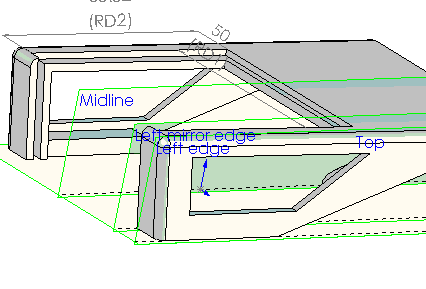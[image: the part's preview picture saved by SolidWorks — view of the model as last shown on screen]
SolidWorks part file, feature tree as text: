
SOLIDWORKS PART (.sldprt)
format: sldprt  version: not decoded by parser v0  size: 412,160 bytes
history: native  units: mm
features: sketch x11, extrude x6, cut_extrude x5, plane x3, fillet x2, mirror x1 + 1 further entry (+9 scaffold rows collapsed)
feature tree (38):
  "Annotations"  RD1=50mm RD2=55.020735mm
  scaffold x9  (default folders/planes/origin — collapsed)
  plane  "Midline"
  plane  "Left edge"  Offset=30.4mm
  plane  "Left mirror edge"  Offset=22mm
  sketch  "Sketch1"  dims[c1.D1=67.88mm c1.D2=33.429mm c1.D3=67.88mm c2.D3=160.0deg c2.D4=25.0mm c2.D5=25.0mm c3.D5=100.0deg c3.D6=25.0mm]
  extrude  "Extrude2"  Depth=2mm
  sketch  "Sketch3"  dims[D1=1.5mm]
  extrude  "Extrude3"  [1 undecoded]
  sketch  "Sketch5"  dims[c1.D1=~23.472852mm c2.D1=~1.335299deg c3.D1=2.0mm c3.D2=~2.004887mm c3.D3=~23.44485mm c4.D1=2.0mm c4.D3=~23.44485mm c5.D3=100.0deg c6.D3=~23.44485mm c7.D3=~0.228426deg c8.D3=~23.44485mm c9.D3=~0.228426deg c10.D3=~23.406929mm c11.D3=~0.03502deg c12.D3=~23.406929mm c13.D3=~0.03502deg c14.D3=2.0mm c14.D4=2.0mm c14.D5=~23.46153mm]
  extrude  "Extrude5"  [1 undecoded]
  sketch  "Sketch11"  dims[D1=4.0mm]
  extrude  "Extrude8"  Depth=5mm
  sketch  "Sketch12"  dims[c1.D1=2.5mm c1.D2=25.0mm c1.D3=30.0mm c2.D2=3.0mm c2.D4=2.0mm c2.D5=50.0mm]
  cut_extrude  "Sideport cut"  Depth=4mm
  mirror  "Mirror1"
  sketch  "Sketch9"  dims[c1.D1=25.0mm c1.D2=40.0mm c1.D3=50.0mm c1.D4=7.0mm c2.D2=25.0mm c2.D4=~4.389902mm c3.D4=90.0deg c4.D4=5.0mm]
  cut_extrude  "Viewport cutout"  Depth=5mm
  sketch  "Sketch10"  dims[c1.D1=4.0mm c1.D2=2.0mm c1.D3=40.0mm c2.D3=~0.615732deg c3.D3=4.0mm c3.D4=4.0mm c3.D5=2.0mm c3.D6=2.0mm c3.D2=5.0mm c4.D4=2.0mm c4.D7=2.0mm c4.D8=5.0mm c4.D9=36.0mm c5.D9=~87.510447deg c5.D7=2.0mm]
  extrude  "Viewport support"  Depth=2mm
  sketch  "Sketch14"  dims[c1.D4=8.0mm c1.D1=36.0mm c1.D2=8.0mm c1.D3=8.0mm c2.D4=~8.164765mm c2.D5=8.0mm]
  extrude  "Left rear screw brace"  Depth=4mm
  sketch  "Sketch16"
  cut_extrude  "Cut-Extrude1"  Depth=5mm
  sketch  "Sketch17"
  cut_extrude  "Cut-Extrude2"  Depth=3mm
  sketch  "Sketch18"
  cut_extrude  "Cut-Extrude3"  Depth=3mm
  fillet  "Fillet1"  Radius=2mm
  fillet  "Fillet2"  Radius=2mm
decode coverage: 19 of 25 modeling features carry decoded parameters; 1 rows unclassified (native names shown)
note: ~ marks probable driven/reference dimensions
note: 2 parameter values undecoded
note: suppression state not decoded; provenance and decode notes live in map.json
